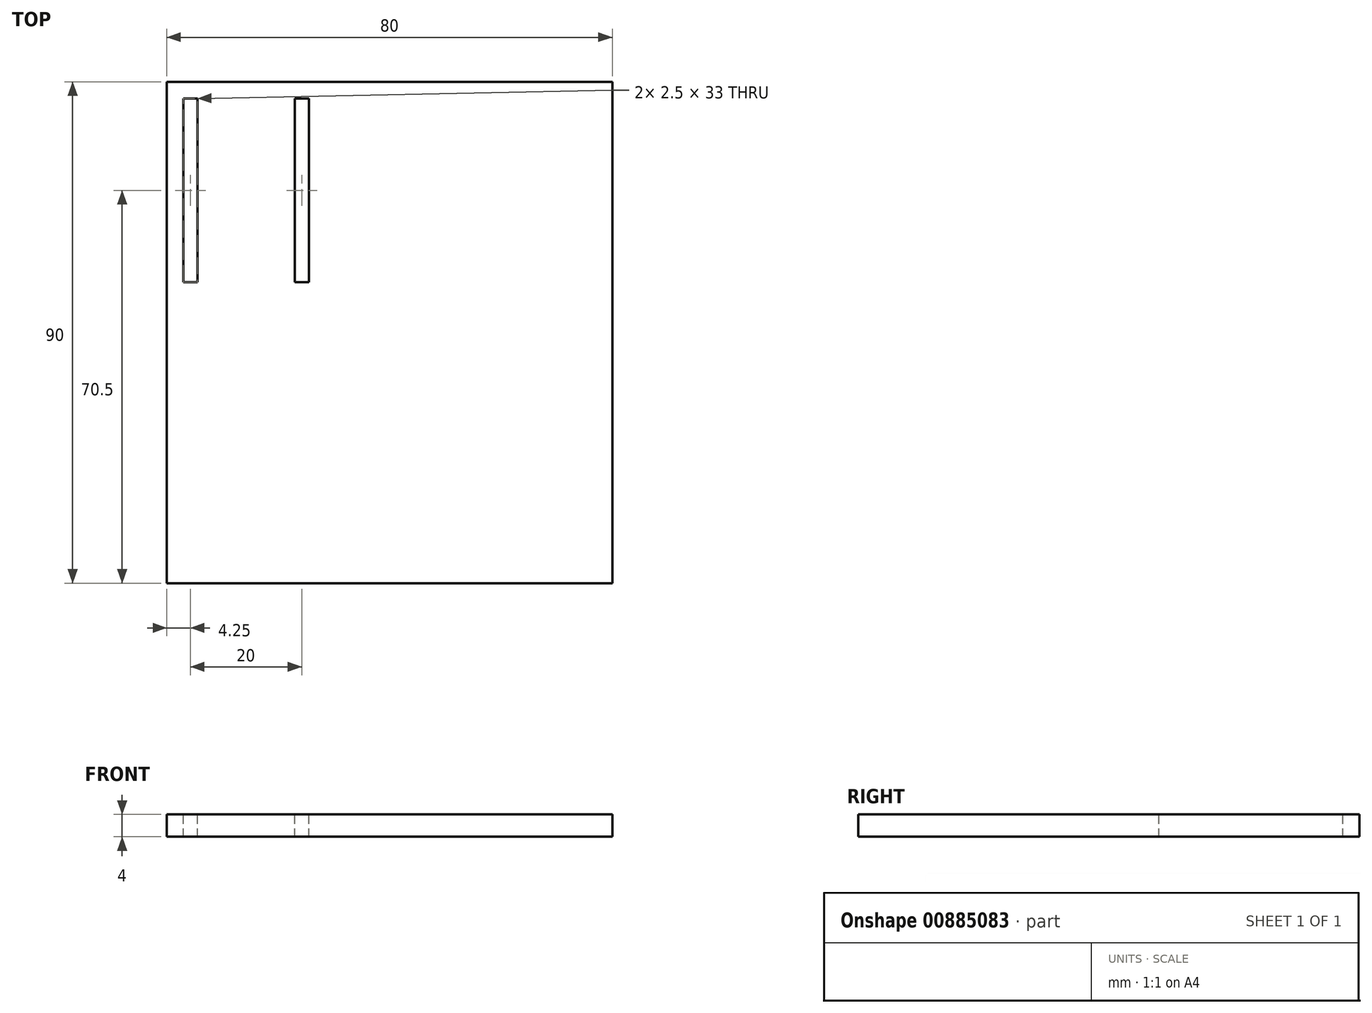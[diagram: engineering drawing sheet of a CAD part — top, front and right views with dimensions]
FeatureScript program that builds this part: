
annotation { "Feature Type Name" : "Feature", "Feature Type Description" : "" }
export const myFeature = defineFeature(function(context is Context, id is Id, definition is map)
    precondition{}
    {
        {
            var Q0;
            Q0=qCreatedBy(makeId("Top.planeOp"),FACE);
            var sketch = newSketch(context, id + "F0", { "sketchPlane" : qUnion([Q0])});
            skLineSegment(sketch, "E0.bottom", {"start": v(-40, 45) * mm, "end": v(40, 45) * mm});
            skLineSegment(sketch, "E0.top", {"start": v(-40, -45) * mm, "end": v(40, -45) * mm});
            skLineSegment(sketch, "E0.left", {"start": v(-40, 45) * mm, "end": v(-40, -45) * mm});
            skLineSegment(sketch, "E0.right", {"start": v(40, 45) * mm, "end": v(40, -45) * mm});
            skPoint(sketch, "E0.middle", {"position": v(0, 0) * mm});
            skSolve(sketch);
        }
        {
            var Q0;
            Q0=makeQuery(id+"F0.imprint","IMPRINT",FACE,{"disambiguationData":[TD([[makeQuery(id+"F0.imprint","IMPRINT",EDGE,{"derivedFrom":sQuery(id+"F0.wireOp",EDGE,"E0.bottom")}),-1.0]])]});
            extrude(context, id + "F1", {"entities" : qUnion([Q0]), "depth" : 4 * mm, "offsetDistance" : 25 * mm});
        }
        {
            var Q0;
            Q0=makeQuery(id+"F1.opExtrude","CAP_FACE",FACE,{"disambiguationData":[OSD([sQuery(id+"F0.wireOp",EDGE,"E0.bottom"),sQuery(id+"F0.wireOp",EDGE,"E0.top"),sQuery(id+"F0.wireOp",EDGE,"E0.left"),sQuery(id+"F0.wireOp",EDGE,"E0.right")])],"isStart":false});
            var sketch = newSketch(context, id + "F2", { "sketchPlane" : qUnion([Q0])});
            skLineSegment(sketch, "E1.bottom", {"start": v(-37, 42) * mm, "end": v(-34.5, 42) * mm});
            skLineSegment(sketch, "E1.top", {"start": v(-37, 9) * mm, "end": v(-34.5, 9) * mm});
            skLineSegment(sketch, "E1.left", {"start": v(-37, 42) * mm, "end": v(-37, 9) * mm});
            skLineSegment(sketch, "E1.right", {"start": v(-34.5, 42) * mm, "end": v(-34.5, 9) * mm});
            skPoint(sketch, "E1.middle", {"position": v(-35.75, 25.5) * mm});
            skLineSegment(sketch, "E2.1.0.0", {"start": v(-14.5, 42) * mm, "end": v(-14.5, 9) * mm});
            skLineSegment(sketch, "E2.1.0.1", {"start": v(-17, 42) * mm, "end": v(-17, 9) * mm});
            skLineSegment(sketch, "E2.1.0.2", {"start": v(-17, 42) * mm, "end": v(-14.5, 42) * mm});
            skLineSegment(sketch, "E2.1.0.3", {"start": v(-17, 9) * mm, "end": v(-14.5, 9) * mm});
            skLineSegment(sketch, "E2.direction1", {"start": v(-34.5, 9) * mm, "end": v(-14.5, 9) * mm, "construction": true});
            skSolve(sketch);
        }
        {
            var Q0;
            Q0 = qSketchRegion(id + "F2", true);
            extrude(context, id + "F3", {"entities" : qUnion([Q0]), "operationType" : NewBodyOperationType.REMOVE, "endBound" : BoundingType.THROUGH_ALL, "oppositeDirection" : true, "depth" : 25 * mm, "offsetDistance" : 25 * mm});
        }
    });
